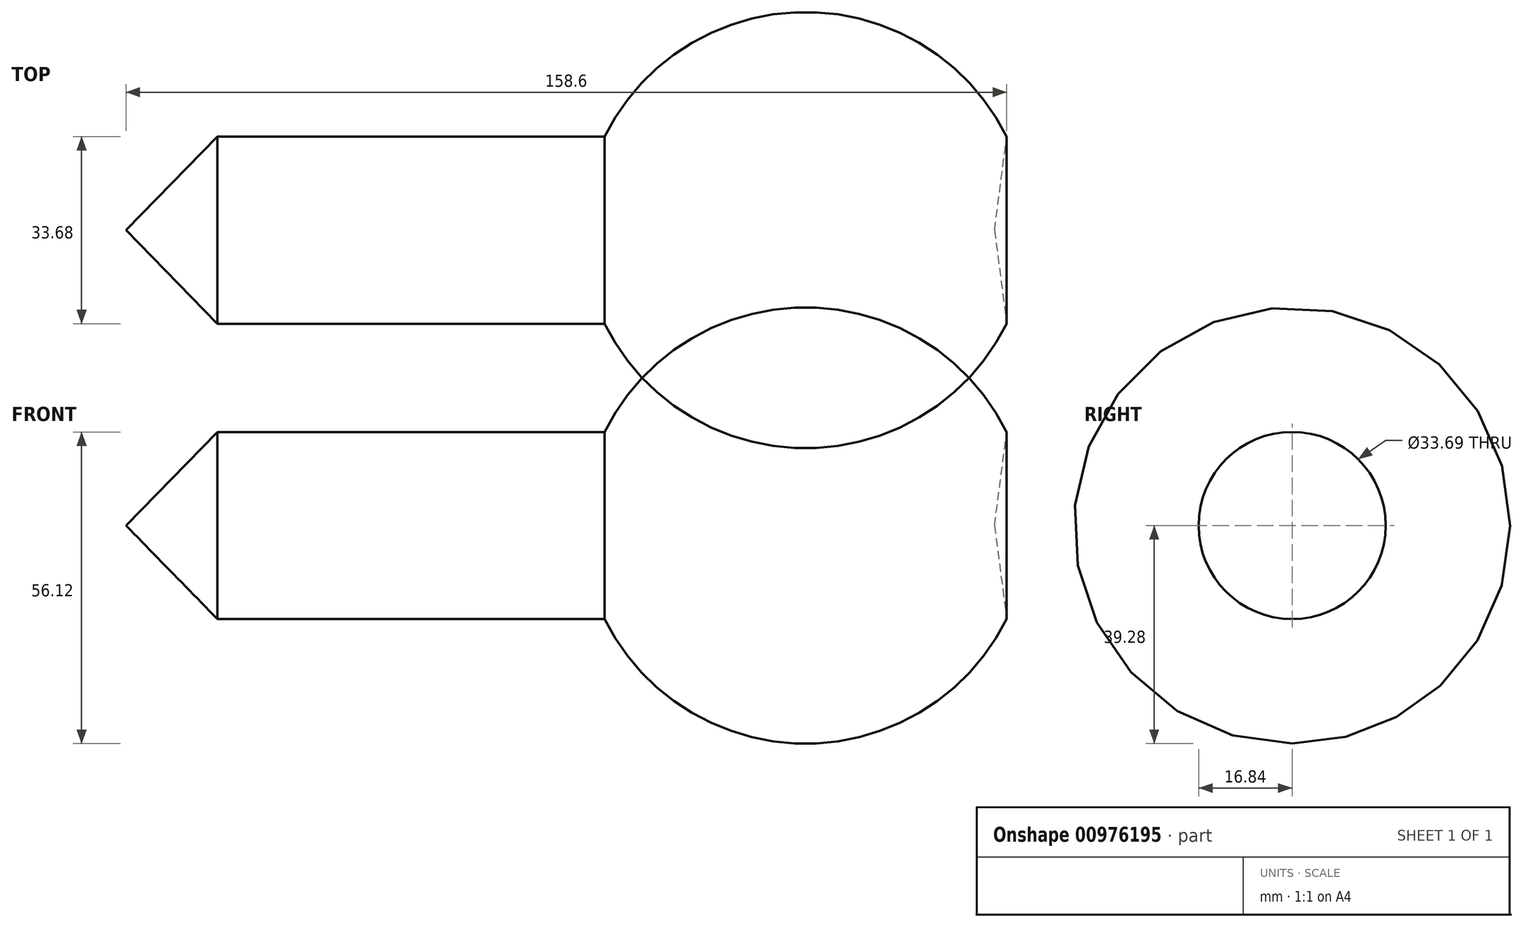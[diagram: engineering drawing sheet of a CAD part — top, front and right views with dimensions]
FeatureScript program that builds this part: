
annotation { "Feature Type Name" : "Feature", "Feature Type Description" : "" }
export const myFeature = defineFeature(function(context is Context, id is Id, definition is map)
    precondition{}
    {
        {
            var Q0;
            Q0=qCreatedBy(makeId("Front.planeOp"),FACE);
            var sketch = newSketch(context, id + "F0", { "sketchPlane" : qUnion([Q0])});
            skLineSegment(sketch, "E0", {"start": v(-94.67, 0) * mm, "end": v(95.21, 0) * mm, "construction": true});
            skLineSegment(sketch, "E1", {"start": v(-61.19, 0) * mm, "end": v(-44.73, 16.84) * mm});
            skLineSegment(sketch, "E2", {"start": v(-44.73, 16.84) * mm, "end": v(24.97, 16.84) * mm});
            skArc(sketch, "E3", {"start": v(97.4, 16.84) * mm, "mid": v(61.19, 39.28) * mm, "end": v(24.97, 16.84) * mm});
            skLineSegment(sketch, "E4", {"start": v(97.4, 16.84) * mm, "end": v(95.21, 0) * mm});
            skSolve(sketch);
        }
        {
            var Q0;
            Q0=sQuery(id+"F0.wireOp",EDGE,"E1");
            var Q1;
            Q1=sQuery(id+"F0.wireOp",EDGE,"E2");
            var Q2;
            Q2=sQuery(id+"F0.wireOp",EDGE,"E3");
            var Q3;
            Q3=sQuery(id+"F0.wireOp",EDGE,"E4");
            var Q4;
            Q4=sQuery(id+"F0.wireOp",EDGE,"E0");
            revolve(context, id + "F1", {"bodyType" : ToolBodyType.SURFACE, "surfaceOperationType" : NewSurfaceOperationType.NEW, "surfaceEntities" : qUnion([Q0, Q1, Q2, Q3]), "axis" : qUnion([Q4]), "revolveType" : RevolveType.FULL});
        }
    });
